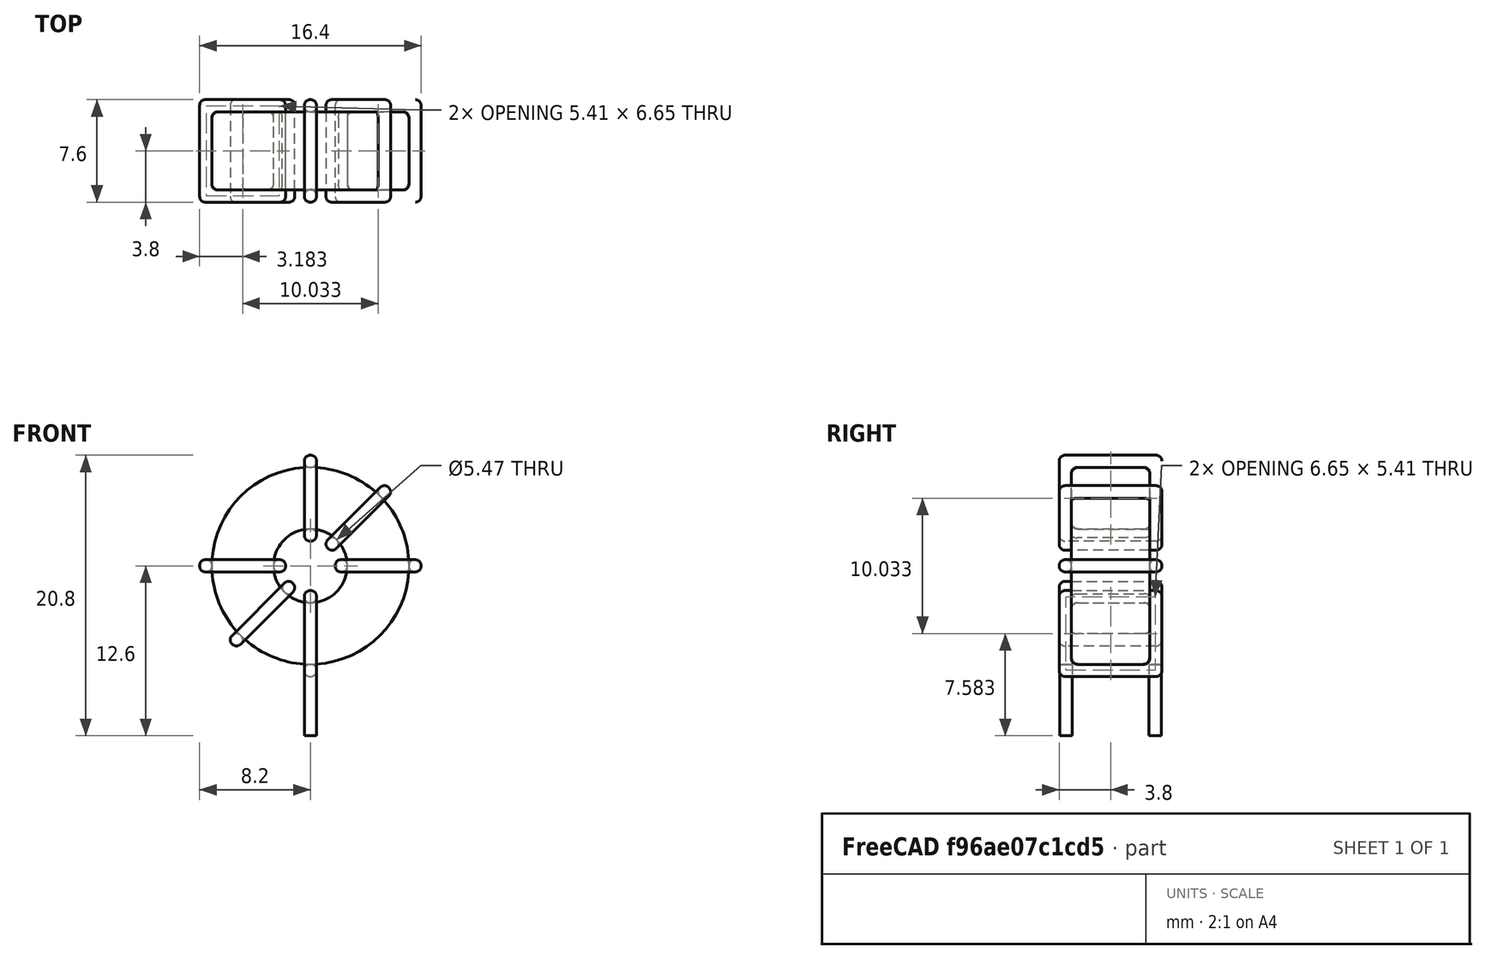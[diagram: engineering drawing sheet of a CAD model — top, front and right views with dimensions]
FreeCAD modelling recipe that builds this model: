
FCSTD DOCUMENT  (FreeCAD 0.16R6703 (Git))
Label: L_Toroid_Vertical_L16.4mm_W7.6mm_P6.60mm_Vishay_TJ3
License: All rights reserved
LicenseURL: http://en.wikipedia.org/wiki/All_rights_reserved
objects: Sketcher::SketchObject×6, PartDesign::Pad×6, PartDesign::Fillet×5, Spreadsheet::Sheet×1
note: 23 computed .brp shape members not serialized (recipe doc carries the construction recipe); baked Part::Feature solids carry a one-line shape summary decoded from their .brp

FEATURE [Spreadsheet::Sheet] Spreadsheet  label="dimensions"
  cells = A1=Wx; B1(Wx)=16.4; C1(WW)=5.466666666666666; D1=16.4; A2=Wy; B2(Wy)=7.6; D2=7.6; A3=RM; B3(RMx)=6.6; C3(RMy)=0; A4=d_wire; B4(d_wire)=0.8999999999999999; A5=H; B5(H)=16.4; A6=offsetx; B6(offsetx)=8.199999999999999
FEATURE [Sketcher::SketchObject] Sketch
  Placement = pos=(0,-3.3,0) rot=(1,0,0;1.5708rad)
  expr: Placement.Base.y = -Spreadsheet.RMx / 2
  expr: Constraints[0] = Spreadsheet.Wx / 2 - Spreadsheet.d_wire
  expr: Constraints[4] = Spreadsheet.WW / 2
  expr: Constraints[2] = Spreadsheet.Wx / 2 + Spreadsheet.d_wire + 0.5
  sketch-geometry (2):
    g0: Circle CenterX=0 CenterY=9.6 CenterZ=0 NormalX=0 NormalY=0 NormalZ=1 Radius=7.3
    g1: Circle CenterX=0 CenterY=9.6 CenterZ=0 NormalX=0 NormalY=0 NormalZ=1 Radius=2.73333
  constraints (5):
    c: Radius(g0) = 7.3
    c: DistanceX(g-1,g0) = 0
    c: DistanceY(g-1,g0) = 9.6
    c: Coincident(g1,g0)
    c: Radius(g1) = 2.73333
FEATURE [PartDesign::Pad] Pad
  Length = 5.8
  Length2 = 100
  Midplane = true
  Placement = pos=(0,-3.3,0) rot=(1,0,0;1.5708rad)
  Sketch = -> Sketch
  Type = 0
  expr: Length = Spreadsheet.Wy - 2 * Spreadsheet.d_wire
FEATURE [Sketcher::SketchObject] Sketch001
  Placement = pos=(0,0,1.4) rot=(0,0,1;0rad)
  expr: Placement.Base.z = 0.5 + Spreadsheet.d_wire
  expr: Constraints[4] = Spreadsheet.RMy
  expr: Constraints[2] = -Spreadsheet.RMx
  expr: Constraints[1] = Spreadsheet.d_wire / 2
  sketch-geometry (2):
    g0: Circle CenterX=0 CenterY=0 CenterZ=0 NormalX=0 NormalY=0 NormalZ=1 Radius=0.45
    g1: Circle CenterX=0 CenterY=-6.6 CenterZ=0 NormalX=0 NormalY=0 NormalZ=1 Radius=0.45
  constraints (5):
    c: Equal(g0,g1)
    c: Radius(g0) = 0.45
    c: DistanceY(g-1,g1) = -6.6
    c: Coincident(g0,g-1)
    c: DistanceX(g-1,g1) = 0
FEATURE [PartDesign::Pad] Pad001
  Length = 0.9
  Length2 = 4.4
  Placement = pos=(0,0,1.4) rot=(0,0,1;0rad)
  Reversed = true
  Sketch = -> Sketch001
  Type = 4
  expr: Length2 = 3.5 + Spreadsheet.d_wire
  expr: Length = Spreadsheet.d_wire
FEATURE [PartDesign::Fillet] Fillet
  Base = -> Pad [Edge6,Edge3,Edge2]
  Placement = pos=(0,-3.3,0) rot=(1,0,0;1.5708rad)
  Radius = 0.5
FEATURE [Sketcher::SketchObject] Sketch003
  Placement = pos=(0,0.5,9.6) rot=(1,0,0;3.14159rad)
  expr: Constraints[18] = Spreadsheet.d_wire
  expr: Constraints[16] = Spreadsheet.d_wire
  expr: Constraints[19] = Spreadsheet.d_wire
  expr: Constraints[17] = Spreadsheet.d_wire
  expr: Placement.Base.y = -1 * (Spreadsheet.RMx - Spreadsheet.Wy) / 2
  expr: Constraints[21] = (Spreadsheet.Wx - Spreadsheet.WW) / 2 - Spreadsheet.d_wire
  expr: Constraints[22] = Spreadsheet.Wx / 2 - Spreadsheet.d_wire
  expr: Constraints[43] = Spreadsheet.d_wire
  expr: Constraints[48] = Spreadsheet.Wx - Spreadsheet.d_wire * 2
  expr: Constraints[49] = Spreadsheet.Wy
  expr: Placement.Base.z = Spreadsheet.Wx / 2 + Spreadsheet.d_wire + 0.5
  sketch-geometry (16):
    g0: LineSegment StartX=-1.83333 StartY=0 StartZ=0 EndX=-8.2 EndY=0 EndZ=0
    g1: LineSegment StartX=-8.2 StartY=0 StartZ=0 EndX=-8.2 EndY=7.6 EndZ=0
    g2: LineSegment StartX=-8.2 StartY=7.6 StartZ=0 EndX=-1.83333 EndY=7.6 EndZ=0
    g3: LineSegment StartX=-1.83333 StartY=7.6 StartZ=0 EndX=-1.83333 EndY=0 EndZ=0
    g4: LineSegment StartX=-7.3 StartY=6.7 StartZ=0 EndX=-2.73333 EndY=6.7 EndZ=0
    g5: LineSegment StartX=-2.73333 StartY=6.7 StartZ=0 EndX=-2.73333 EndY=0.9 EndZ=0
    g6: LineSegment StartX=-2.73333 StartY=0.9 StartZ=0 EndX=-7.3 EndY=0.9 EndZ=0
    g7: LineSegment StartX=-7.3 StartY=0.9 StartZ=0 EndX=-7.3 EndY=6.7 EndZ=0
    g8: LineSegment StartX=1.83333 StartY=7.6 StartZ=0 EndX=8.2 EndY=7.6 EndZ=0
    g9: LineSegment StartX=8.2 StartY=7.6 StartZ=0 EndX=8.2 EndY=0 EndZ=0
    g10: LineSegment StartX=8.2 StartY=0 StartZ=0 EndX=1.83333 EndY=0 EndZ=0
    g11: LineSegment StartX=1.83333 StartY=0 StartZ=0 EndX=1.83333 EndY=7.6 EndZ=0
    g12: LineSegment StartX=2.73333 StartY=6.7 StartZ=0 EndX=7.3 EndY=6.7 EndZ=0
    g13: LineSegment StartX=7.3 StartY=6.7 StartZ=0 EndX=7.3 EndY=0.9 EndZ=0
    g14: LineSegment StartX=7.3 StartY=0.9 StartZ=0 EndX=2.73333 EndY=0.9 EndZ=0
    g15: LineSegment StartX=2.73333 StartY=0.9 StartZ=0 EndX=2.73333 EndY=6.7 EndZ=0
  constraints (50):
    c: Horizontal(g0)
    c: Coincident(g1,g0)
    c: Vertical(g1)
    c: Coincident(g2,g1)
    c: Horizontal(g2)
    c: Coincident(g3,g2)
    c: Coincident(g3,g0)
    c: Vertical(g3)
    c: Coincident(g4,g5)
    c: Coincident(g5,g6)
    c: Coincident(g6,g7)
    c: Coincident(g7,g4)
    c: Horizontal(g4)
    c: Horizontal(g6)
    c: Vertical(g5)
    c: Vertical(g7)
    c: DistanceX(g1,g4) = 0.9
    c: DistanceY(g4,g1) = 0.9
    c: DistanceX(g5,g0) = 0.9
    c: DistanceY(g0,g5) = 0.9
    c: DistanceY(g-1,g0) = 0
    c: DistanceX(g6,g6) = 4.56667
    c: DistanceX(g6,g-1) = 7.3
    c: Coincident(g8,g9)
    c: Coincident(g9,g10)
    c: Coincident(g10,g11)
    c: Coincident(g11,g8)
    c: Horizontal(g8)
    c: Horizontal(g10)
    c: Vertical(g9)
    c: Vertical(g11)
    c: Coincident(g12,g13)
    c: Coincident(g13,g14)
    c: Coincident(g14,g15)
    c: Coincident(g15,g12)
    c: Horizontal(g12)
    c: Horizontal(g14)
    c: Vertical(g13)
    c: Vertical(g15)
    c: DistanceY(g8,g2) = 0
    c: DistanceY(g10,g0) = 0
    c: DistanceY(g14,g5) = 0
    c: DistanceY(g12,g4) = 0
    c: DistanceX(g8,g12) = 0.9
    c: Equal(g8,g2)
    c: Equal(g12,g4)
    c: Equal(g9,g1)
    c: Equal(g13,g7)
    c: DistanceX(g4,g12) = 14.6
    c: DistanceY(g0,g1) = 7.6
FEATURE [PartDesign::Pad] Pad002
  Length = 0.9
  Length2 = 100
  Midplane = true
  Placement = pos=(0,0.5,9.6) rot=(1,0,0;3.14159rad)
  Sketch = -> Sketch003
  Type = 0
  expr: Length = Spreadsheet.d_wire
FEATURE [PartDesign::Fillet] Fillet001
  Base = -> Pad002 [Edge38,Edge41,Edge42,Edge43,Edge29,Edge32,Edge33,Edge34,Edge25,Edge35,Edge36,Edge13,Edge14,Edge15,Edge16,Edge17,Edge18,Edge19,Edge1,Edge2,Edge3,Edge4,Edge5,Edge6,Edge7,Edge37,Edge39,Edge40,Edge20,Edge23,Edge24,Edge21,Edge22,Edge8,Edge9,Edge10,Edge11,Edge12,Edge26,Edge27,+8 more]
  Placement = pos=(0,0.5,9.6) rot=(1,0,0;3.14159rad)
  Radius = 0.423
  expr: Radius = Spreadsheet.d_wire * 0.47
FEATURE [Sketcher::SketchObject] Sketch004
  Placement = pos=(0,0.5,9.6) rot=(0.92388,0,0.382683;3.14159rad)
  expr: Constraints[18] = Spreadsheet.d_wire
  expr: Constraints[16] = Spreadsheet.d_wire
  expr: Constraints[19] = Spreadsheet.d_wire
  expr: Constraints[17] = Spreadsheet.d_wire
  expr: Placement.Base.y = -1 * (Spreadsheet.RMx - Spreadsheet.Wy) / 2
  expr: Constraints[21] = (Spreadsheet.Wx - Spreadsheet.WW) / 2 - Spreadsheet.d_wire
  expr: Constraints[22] = Spreadsheet.Wx / 2 - Spreadsheet.d_wire
  expr: Constraints[43] = Spreadsheet.d_wire
  expr: Constraints[48] = Spreadsheet.Wx - 2 * Spreadsheet.d_wire
  expr: Constraints[49] = Spreadsheet.Wy
  expr: Placement.Base.z = Spreadsheet.Wx / 2 + Spreadsheet.d_wire + 0.5
  sketch-geometry (16):
    g0: LineSegment StartX=-1.83333 StartY=0 StartZ=0 EndX=-8.2 EndY=0 EndZ=0
    g1: LineSegment StartX=-8.2 StartY=0 StartZ=0 EndX=-8.2 EndY=7.6 EndZ=0
    g2: LineSegment StartX=-8.2 StartY=7.6 StartZ=0 EndX=-1.83333 EndY=7.6 EndZ=0
    g3: LineSegment StartX=-1.83333 StartY=7.6 StartZ=0 EndX=-1.83333 EndY=0 EndZ=0
    g4: LineSegment StartX=-7.3 StartY=6.7 StartZ=0 EndX=-2.73333 EndY=6.7 EndZ=0
    g5: LineSegment StartX=-2.73333 StartY=6.7 StartZ=0 EndX=-2.73333 EndY=0.9 EndZ=0
    g6: LineSegment StartX=-2.73333 StartY=0.9 StartZ=0 EndX=-7.3 EndY=0.9 EndZ=0
    g7: LineSegment StartX=-7.3 StartY=0.9 StartZ=0 EndX=-7.3 EndY=6.7 EndZ=0
    g8: LineSegment StartX=1.83333 StartY=7.6 StartZ=0 EndX=8.2 EndY=7.6 EndZ=0
    g9: LineSegment StartX=8.2 StartY=7.6 StartZ=0 EndX=8.2 EndY=0 EndZ=0
    g10: LineSegment StartX=8.2 StartY=0 StartZ=0 EndX=1.83333 EndY=0 EndZ=0
    g11: LineSegment StartX=1.83333 StartY=0 StartZ=0 EndX=1.83333 EndY=7.6 EndZ=0
    g12: LineSegment StartX=2.73333 StartY=6.7 StartZ=0 EndX=7.3 EndY=6.7 EndZ=0
    g13: LineSegment StartX=7.3 StartY=6.7 StartZ=0 EndX=7.3 EndY=0.9 EndZ=0
    g14: LineSegment StartX=7.3 StartY=0.9 StartZ=0 EndX=2.73333 EndY=0.9 EndZ=0
    g15: LineSegment StartX=2.73333 StartY=0.9 StartZ=0 EndX=2.73333 EndY=6.7 EndZ=0
  constraints (50):
    c: Horizontal(g0)
    c: Coincident(g1,g0)
    c: Vertical(g1)
    c: Coincident(g2,g1)
    c: Horizontal(g2)
    c: Coincident(g3,g2)
    c: Coincident(g3,g0)
    c: Vertical(g3)
    c: Coincident(g4,g5)
    c: Coincident(g5,g6)
    c: Coincident(g6,g7)
    c: Coincident(g7,g4)
    c: Horizontal(g4)
    c: Horizontal(g6)
    c: Vertical(g5)
    c: Vertical(g7)
    c: DistanceX(g1,g4) = 0.9
    c: DistanceY(g4,g1) = 0.9
    c: DistanceX(g5,g0) = 0.9
    c: DistanceY(g0,g5) = 0.9
    c: DistanceY(g-1,g0) = 0
    c: DistanceX(g6,g6) = 4.56667
    c: DistanceX(g6,g-1) = 7.3
    c: Coincident(g8,g9)
    c: Coincident(g9,g10)
    c: Coincident(g10,g11)
    c: Coincident(g11,g8)
    c: Horizontal(g8)
    c: Horizontal(g10)
    c: Vertical(g9)
    c: Vertical(g11)
    c: Coincident(g12,g13)
    c: Coincident(g13,g14)
    c: Coincident(g14,g15)
    c: Coincident(g15,g12)
    c: Horizontal(g12)
    c: Horizontal(g14)
    c: Vertical(g13)
    c: Vertical(g15)
    c: DistanceY(g8,g2) = 0
    c: DistanceY(g10,g0) = 0
    c: DistanceY(g14,g5) = 0
    c: DistanceY(g12,g4) = 0
    c: DistanceX(g8,g12) = 0.9
    c: Equal(g8,g2)
    c: Equal(g12,g4)
    c: Equal(g9,g1)
    c: Equal(g13,g7)
    c: DistanceX(g4,g12) = 14.6
    c: DistanceY(g0,g1) = 7.6
FEATURE [PartDesign::Pad] Pad003
  Length = 0.9
  Length2 = 100
  Midplane = true
  Placement = pos=(0,0.5,9.6) rot=(0.92388,0,0.382683;3.14159rad)
  Sketch = -> Sketch004
  Type = 0
  expr: Length = Spreadsheet.d_wire
FEATURE [PartDesign::Fillet] Fillet002
  Base = -> Pad003 [Edge38,Edge41,Edge42,Edge43,Edge29,Edge32,Edge33,Edge34,Edge25,Edge35,Edge36,Edge13,Edge14,Edge15,Edge16,Edge17,Edge18,Edge19,Edge1,Edge2,Edge3,Edge4,Edge5,Edge6,Edge7,Edge37,Edge39,Edge40,Edge20,Edge23,Edge24,Edge21,Edge22,Edge8,Edge9,Edge10,Edge11,Edge12,Edge26,Edge27,+8 more]
  Placement = pos=(0,0.5,9.6) rot=(0.92388,0,0.382683;3.14159rad)
  Radius = 0.423
  expr: Radius = Spreadsheet.d_wire * 0.47
FEATURE [Sketcher::SketchObject] Sketch005
  Placement = pos=(0,0.5,9.6) rot=(0.92388,0,-0.382683;3.14159rad)
  expr: Constraints[18] = Spreadsheet.d_wire
  expr: Constraints[16] = Spreadsheet.d_wire
  expr: Constraints[19] = Spreadsheet.d_wire
  expr: Constraints[17] = Spreadsheet.d_wire
  expr: Placement.Base.y = -1 * (Spreadsheet.RMx - Spreadsheet.Wy) / 2
  expr: Constraints[21] = (Spreadsheet.Wx - Spreadsheet.WW) / 2 - Spreadsheet.d_wire
  expr: Constraints[22] = Spreadsheet.Wx / 2 - Spreadsheet.d_wire
  expr: Constraints[43] = Spreadsheet.d_wire
  expr: Constraints[48] = Spreadsheet.Wx - 2 * Spreadsheet.d_wire
  expr: Constraints[49] = Spreadsheet.Wy
  expr: Placement.Base.z = Spreadsheet.Wx / 2 + Spreadsheet.d_wire + 0.5
  sketch-geometry (16):
    g0: LineSegment StartX=-1.83333 StartY=0 StartZ=0 EndX=-8.2 EndY=0 EndZ=0
    g1: LineSegment StartX=-8.2 StartY=0 StartZ=0 EndX=-8.2 EndY=7.6 EndZ=0
    g2: LineSegment StartX=-8.2 StartY=7.6 StartZ=0 EndX=-1.83333 EndY=7.6 EndZ=0
    g3: LineSegment StartX=-1.83333 StartY=7.6 StartZ=0 EndX=-1.83333 EndY=0 EndZ=0
    g4: LineSegment StartX=-7.3 StartY=6.7 StartZ=0 EndX=-2.73333 EndY=6.7 EndZ=0
    g5: LineSegment StartX=-2.73333 StartY=6.7 StartZ=0 EndX=-2.73333 EndY=0.9 EndZ=0
    g6: LineSegment StartX=-2.73333 StartY=0.9 StartZ=0 EndX=-7.3 EndY=0.9 EndZ=0
    g7: LineSegment StartX=-7.3 StartY=0.9 StartZ=0 EndX=-7.3 EndY=6.7 EndZ=0
    g8: LineSegment StartX=1.83333 StartY=7.6 StartZ=0 EndX=8.2 EndY=7.6 EndZ=0
    g9: LineSegment StartX=8.2 StartY=7.6 StartZ=0 EndX=8.2 EndY=0 EndZ=0
    g10: LineSegment StartX=8.2 StartY=0 StartZ=0 EndX=1.83333 EndY=0 EndZ=0
    g11: LineSegment StartX=1.83333 StartY=0 StartZ=0 EndX=1.83333 EndY=7.6 EndZ=0
    g12: LineSegment StartX=2.73333 StartY=6.7 StartZ=0 EndX=7.3 EndY=6.7 EndZ=0
    g13: LineSegment StartX=7.3 StartY=6.7 StartZ=0 EndX=7.3 EndY=0.9 EndZ=0
    g14: LineSegment StartX=7.3 StartY=0.9 StartZ=0 EndX=2.73333 EndY=0.9 EndZ=0
    g15: LineSegment StartX=2.73333 StartY=0.9 StartZ=0 EndX=2.73333 EndY=6.7 EndZ=0
  constraints (50):
    c: Horizontal(g0)
    c: Coincident(g1,g0)
    c: Vertical(g1)
    c: Coincident(g2,g1)
    c: Horizontal(g2)
    c: Coincident(g3,g2)
    c: Coincident(g3,g0)
    c: Vertical(g3)
    c: Coincident(g4,g5)
    c: Coincident(g5,g6)
    c: Coincident(g6,g7)
    c: Coincident(g7,g4)
    c: Horizontal(g4)
    c: Horizontal(g6)
    c: Vertical(g5)
    c: Vertical(g7)
    c: DistanceX(g1,g4) = 0.9
    c: DistanceY(g4,g1) = 0.9
    c: DistanceX(g5,g0) = 0.9
    c: DistanceY(g0,g5) = 0.9
    c: DistanceY(g-1,g0) = 0
    c: DistanceX(g6,g6) = 4.56667
    c: DistanceX(g6,g-1) = 7.3
    c: Coincident(g8,g9)
    c: Coincident(g9,g10)
    c: Coincident(g10,g11)
    c: Coincident(g11,g8)
    c: Horizontal(g8)
    c: Horizontal(g10)
    c: Vertical(g9)
    c: Vertical(g11)
    c: Coincident(g12,g13)
    c: Coincident(g13,g14)
    c: Coincident(g14,g15)
    c: Coincident(g15,g12)
    c: Horizontal(g12)
    c: Horizontal(g14)
    c: Vertical(g13)
    c: Vertical(g15)
    c: DistanceY(g8,g2) = 0
    c: DistanceY(g10,g0) = 0
    c: DistanceY(g14,g5) = 0
    c: DistanceY(g12,g4) = 0
    c: DistanceX(g8,g12) = 0.9
    c: Equal(g8,g2)
    c: Equal(g12,g4)
    c: Equal(g9,g1)
    c: Equal(g13,g7)
    c: DistanceX(g4,g12) = 14.6
    c: DistanceY(g0,g1) = 7.6
FEATURE [PartDesign::Pad] Pad004
  Length = 0.9
  Length2 = 100
  Midplane = true
  Placement = pos=(0,0.5,9.6) rot=(0.92388,0,-0.382683;3.14159rad)
  Sketch = -> Sketch005
  Type = 0
  expr: Length = Spreadsheet.d_wire
FEATURE [PartDesign::Fillet] Fillet003
  Base = -> Pad004 [Edge38,Edge41,Edge42,Edge43,Edge29,Edge32,Edge33,Edge34,Edge25,Edge35,Edge36,Edge13,Edge14,Edge15,Edge16,Edge17,Edge18,Edge19,Edge1,Edge2,Edge3,Edge4,Edge5,Edge6,Edge7,Edge37,Edge39,Edge40,Edge20,Edge23,Edge24,Edge21,Edge22,Edge8,Edge9,Edge10,Edge11,Edge12,Edge26,Edge27,+8 more]
  Placement = pos=(0,0.5,9.6) rot=(0.92388,0,-0.382683;3.14159rad)
  Radius = 0.423
  expr: Radius = Spreadsheet.d_wire * 0.47
FEATURE [Sketcher::SketchObject] Sketch006
  Placement = pos=(0,0.5,9.6) rot=(0.707107,0,0.707107;3.14159rad)
  expr: Constraints[18] = Spreadsheet.d_wire
  expr: Constraints[16] = Spreadsheet.d_wire
  expr: Constraints[19] = Spreadsheet.d_wire
  expr: Constraints[17] = Spreadsheet.d_wire
  expr: Placement.Base.y = -1 * (Spreadsheet.RMx - Spreadsheet.Wy) / 2
  expr: Constraints[21] = (Spreadsheet.Wx - Spreadsheet.WW) / 2 - Spreadsheet.d_wire
  expr: Constraints[22] = Spreadsheet.Wx / 2 - Spreadsheet.d_wire
  expr: Constraints[43] = Spreadsheet.d_wire
  expr: Constraints[48] = Spreadsheet.Wx - Spreadsheet.d_wire * 2
  expr: Constraints[49] = Spreadsheet.Wy
  expr: Placement.Base.z = Spreadsheet.Wx / 2 + Spreadsheet.d_wire + 0.5
  sketch-geometry (16):
    g0: LineSegment StartX=-1.83333 StartY=0 StartZ=0 EndX=-8.2 EndY=0 EndZ=0
    g1: LineSegment StartX=-8.2 StartY=0 StartZ=0 EndX=-8.2 EndY=7.6 EndZ=0
    g2: LineSegment StartX=-8.2 StartY=7.6 StartZ=0 EndX=-1.83333 EndY=7.6 EndZ=0
    g3: LineSegment StartX=-1.83333 StartY=7.6 StartZ=0 EndX=-1.83333 EndY=0 EndZ=0
    g4: LineSegment StartX=-7.3 StartY=6.7 StartZ=0 EndX=-2.73333 EndY=6.7 EndZ=0
    g5: LineSegment StartX=-2.73333 StartY=6.7 StartZ=0 EndX=-2.73333 EndY=0.9 EndZ=0
    g6: LineSegment StartX=-2.73333 StartY=0.9 StartZ=0 EndX=-7.3 EndY=0.9 EndZ=0
    g7: LineSegment StartX=-7.3 StartY=0.9 StartZ=0 EndX=-7.3 EndY=6.7 EndZ=0
    g8: LineSegment StartX=1.83333 StartY=7.6 StartZ=0 EndX=8.2 EndY=7.6 EndZ=0
    g9: LineSegment StartX=8.2 StartY=7.6 StartZ=0 EndX=8.2 EndY=0 EndZ=0
    g10: LineSegment StartX=8.2 StartY=0 StartZ=0 EndX=1.83333 EndY=0 EndZ=0
    g11: LineSegment StartX=1.83333 StartY=0 StartZ=0 EndX=1.83333 EndY=7.6 EndZ=0
    g12: LineSegment StartX=2.73333 StartY=6.7 StartZ=0 EndX=7.3 EndY=6.7 EndZ=0
    g13: LineSegment StartX=7.3 StartY=6.7 StartZ=0 EndX=7.3 EndY=0.9 EndZ=0
    g14: LineSegment StartX=7.3 StartY=0.9 StartZ=0 EndX=2.73333 EndY=0.9 EndZ=0
    g15: LineSegment StartX=2.73333 StartY=0.9 StartZ=0 EndX=2.73333 EndY=6.7 EndZ=0
  constraints (50):
    c: Horizontal(g0)
    c: Coincident(g1,g0)
    c: Vertical(g1)
    c: Coincident(g2,g1)
    c: Horizontal(g2)
    c: Coincident(g3,g2)
    c: Coincident(g3,g0)
    c: Vertical(g3)
    c: Coincident(g4,g5)
    c: Coincident(g5,g6)
    c: Coincident(g6,g7)
    c: Coincident(g7,g4)
    c: Horizontal(g4)
    c: Horizontal(g6)
    c: Vertical(g5)
    c: Vertical(g7)
    c: DistanceX(g1,g4) = 0.9
    c: DistanceY(g4,g1) = 0.9
    c: DistanceX(g5,g0) = 0.9
    c: DistanceY(g0,g5) = 0.9
    c: DistanceY(g-1,g0) = 0
    c: DistanceX(g6,g6) = 4.56667
    c: DistanceX(g6,g-1) = 7.3
    c: Coincident(g8,g9)
    c: Coincident(g9,g10)
    c: Coincident(g10,g11)
    c: Coincident(g11,g8)
    c: Horizontal(g8)
    c: Horizontal(g10)
    c: Vertical(g9)
    c: Vertical(g11)
    c: Coincident(g12,g13)
    c: Coincident(g13,g14)
    c: Coincident(g14,g15)
    c: Coincident(g15,g12)
    c: Horizontal(g12)
    c: Horizontal(g14)
    c: Vertical(g13)
    c: Vertical(g15)
    c: DistanceY(g8,g2) = 0
    c: DistanceY(g10,g0) = 0
    c: DistanceY(g14,g5) = 0
    c: DistanceY(g12,g4) = 0
    c: DistanceX(g8,g12) = 0.9
    c: Equal(g8,g2)
    c: Equal(g12,g4)
    c: Equal(g9,g1)
    c: Equal(g13,g7)
    c: DistanceX(g4,g12) = 14.6
    c: DistanceY(g0,g1) = 7.6
FEATURE [PartDesign::Pad] Pad005
  Length = 0.9
  Length2 = 100
  Midplane = true
  Placement = pos=(0,0.5,9.6) rot=(0.707107,0,0.707107;3.14159rad)
  Sketch = -> Sketch006
  Type = 0
  expr: Length = Spreadsheet.d_wire
FEATURE [PartDesign::Fillet] Fillet004
  Base = -> Pad005 [Edge38,Edge41,Edge42,Edge43,Edge29,Edge32,Edge33,Edge34,Edge25,Edge35,Edge36,Edge13,Edge14,Edge15,Edge16,Edge17,Edge18,Edge19,Edge1,Edge2,Edge3,Edge4,Edge5,Edge6,Edge7,Edge37,Edge39,Edge40,Edge20,Edge23,Edge24,Edge21,Edge22,Edge8,Edge9,Edge10,Edge11,Edge12,Edge26,Edge27,+8 more]
  Placement = pos=(0,0.5,9.6) rot=(0.707107,0,0.707107;3.14159rad)
  Radius = 0.423
  expr: Radius = Spreadsheet.d_wire * 0.47
